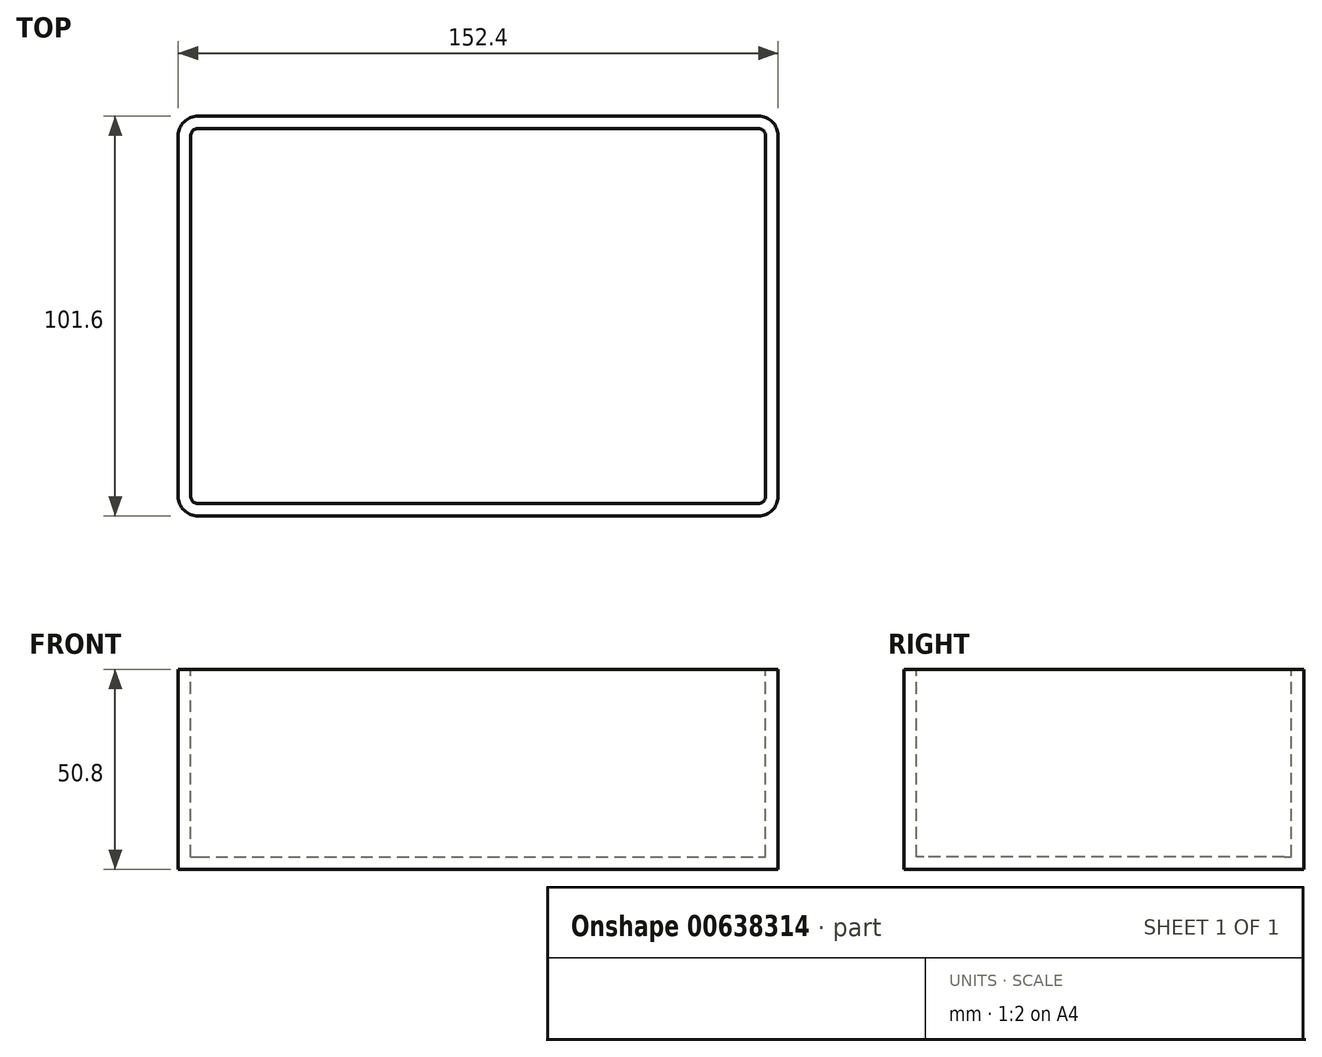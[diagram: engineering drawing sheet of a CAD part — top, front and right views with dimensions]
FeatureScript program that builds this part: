
annotation { "Feature Type Name" : "Feature", "Feature Type Description" : "" }
export const myFeature = defineFeature(function(context is Context, id is Id, definition is map)
    precondition{}
    {
        {
            var Q0;
            Q0=qCreatedBy(makeId("Top.planeOp"),FACE);
            var sketch = newSketch(context, id + "F0", { "sketchPlane" : qUnion([Q0])});
            skLineSegment(sketch, "E0.bottom", {"start": v(-79.33, 52.89) * mm, "end": v(73.07, 52.89) * mm});
            skLineSegment(sketch, "E0.top", {"start": v(-79.33, -48.71) * mm, "end": v(73.07, -48.71) * mm});
            skLineSegment(sketch, "E0.left", {"start": v(-79.33, 52.89) * mm, "end": v(-79.33, -48.71) * mm});
            skLineSegment(sketch, "E0.right", {"start": v(73.07, 52.89) * mm, "end": v(73.07, -48.71) * mm});
            skLineSegment(sketch, "E1", {"start": v(-79.33, 52.89) * mm, "end": v(73.07, -48.71) * mm});
            skSolve(sketch);
        }
        {
            var Q0;
            Q0 = qSketchRegion(id + "F0", true);
            extrude(context, id + "F1", {"entities" : qUnion([Q0]), "depth" : 50.8 * mm, "offsetDistance" : 25.4 * mm});
        }
        {
            var Q0;
            Q0=makeQuery(id+"F1.opExtrude","SWEPT_EDGE",EDGE,{"disambiguationData":[OSD([sQuery(id+"F0.wireOp",EDGE,"E0.top"),sQuery(id+"F0.wireOp",EDGE,"E0.left")])]});
            var Q1;
            Q1=makeQuery(id+"F1.opExtrude","SWEPT_EDGE",EDGE,{"disambiguationData":[OSD([sQuery(id+"F0.wireOp",EDGE,"E0.top"),sQuery(id+"F0.wireOp",EDGE,"E0.right"),sQuery(id+"F0.wireOp",EDGE,"E1")])]});
            var Q2;
            Q2=makeQuery(id+"F1.opExtrude","SWEPT_EDGE",EDGE,{"disambiguationData":[OSD([sQuery(id+"F0.wireOp",EDGE,"E0.bottom"),sQuery(id+"F0.wireOp",EDGE,"E0.right")])]});
            var Q3;
            Q3=makeQuery(id+"F1.opExtrude","SWEPT_EDGE",EDGE,{"disambiguationData":[OSD([sQuery(id+"F0.wireOp",EDGE,"E0.bottom"),sQuery(id+"F0.wireOp",EDGE,"E0.left"),sQuery(id+"F0.wireOp",EDGE,"E1")])]});
            fillet(context, id + "F2", {"entities" : qUnion([Q0, Q1, Q2, Q3]), "radius" : 5 * mm, "tangentPropagation" : true, "allowEdgeOverflow" : false});
        }
        {
            var Q0;
            Q0=makeQuery(id+"F1.opExtrude","CAP_FACE",FACE,{"disambiguationData":[OSD([sQuery(id+"F0.wireOp",EDGE,"E0.bottom"),sQuery(id+"F0.wireOp",EDGE,"E0.top"),sQuery(id+"F0.wireOp",EDGE,"E0.left"),sQuery(id+"F0.wireOp",EDGE,"E0.right")])],"isStart":false});
            shell(context, id + "F3", {"entities" : qUnion([Q0]), "thickness" : 3.17 * mm});
        }
    });
